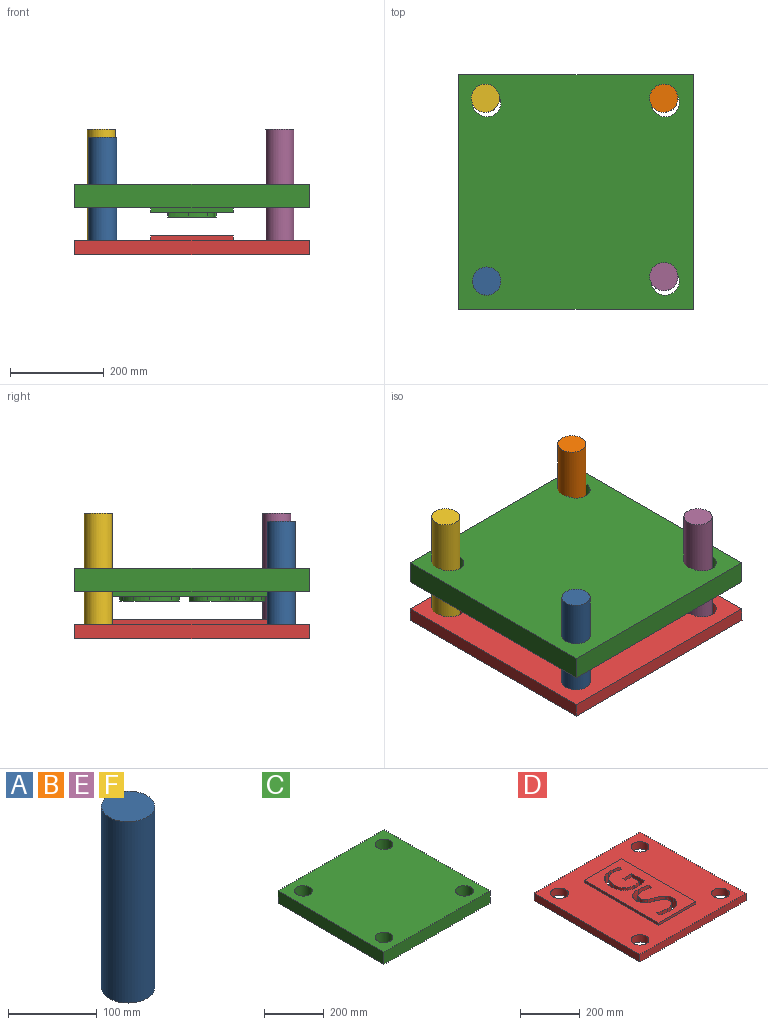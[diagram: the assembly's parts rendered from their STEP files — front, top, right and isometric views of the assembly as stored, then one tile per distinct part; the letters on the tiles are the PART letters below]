
ASSEMBLY  parts=6 mates=2
PART A: 3 faces, bbox 60x60x250 mm
  f0: cylinder r=30mm len=250mm, axis (0,0,-1), area 47123.9mm2, adj f1,f2
  f1: plane 60x60mm, normal (0,0,1), area 2827.4mm2, adj f0
  f2: plane 60x60mm, normal (0,0,-1), area 2827.4mm2, adj f0
PART B: same geometry as A
PART C: 62 faces, bbox 500x500x70 mm
  f0: plane 500x500mm, normal (0,0,-1), area 177440.3mm2, adj f1,f2,f3,f4,f5,f6,f7,f8
  f1: plane 500x50mm, normal (0,-1,0), area 25000mm2, adj f0,f2,f8,f9
  f2: plane 500x50mm, normal (1,0,0), area 25000mm2, adj f0,f1,f3,f9
  f3: plane 500x50mm, normal (0,1,0), area 25000mm2, adj f0,f2,f8,f9
  f4: cylinder r=30mm len=60mm, axis (0,0,1), area 9424.8mm2, adj f0,f9
  f5: cylinder r=30mm len=60mm, axis (0,0,1), area 9424.8mm2, adj f0,f9
  f6: cylinder r=30mm len=60mm, axis (0,0,1), area 9424.8mm2, adj f0,f9
  f7: cylinder r=30mm len=60mm, axis (0,0,1), area 9424.8mm2, adj f0,f9
  f8: plane 500x50mm, normal (-1,0,0), area 25000mm2, adj f0,f1,f3,f9
  f9: plane 500x500mm, normal (0,0,1), area 238690.3mm2, adj f1,f2,f3,f4,f5,f6,f7,f8
  f10: plane 175x10mm, normal (0,-1,0), area 1750mm2, adj f0,f11,f13,f14
  f11: plane 350x10mm, normal (1,0,0), area 3500mm2, adj f0,f10,f12,f14
  f12: plane 175x10mm, normal (0,1,0), area 1750mm2, adj f0,f11,f13,f14
  f13: plane 350x10mm, normal (-1,0,0), area 3500mm2, adj f0,f10,f12,f14
  f14: plane 350x175mm, normal (0,0,-1), area 50837.5mm2, adj f10,f11,f12,f13,f15,f16,f17,f18
  f15: plane 42.15x10mm, normal (0,1,0), area 421.5mm2, adj f14,f16,f26,f35
  f16: plane 12.89x10mm, normal (-1,0,0), area 128.9mm2, adj f14,f15,f27,f35
  f17: plane 12.73x10mm, normal (0.92,-0.4,0), area 139mm2, adj f14,f18,f34,f35
  f18: extruded ~36.99x10mm, area 379.6mm2, adj f14,f17,f19,f35
  f19: extruded ~34.15x10mm, area 353.5mm2, adj f14,f18,f20,f35
  f20: extruded ~22.35x22.21mm, area 320mm2, adj f14,f19,f21,f35
  f21: extruded ~33.9x10mm, area 351.3mm2, adj f14,f20,f22,f35
  f22: extruded ~46.94x15.69mm, area 507.1mm2, adj f14,f21,f23,f35
  f23: extruded ~43.83x16.76mm, area 483.3mm2, adj f14,f22,f24,f35
  f24: extruded ~23.58x10mm, area 236.6mm2, adj f14,f23,f25,f35
  f25: extruded ~20.03x10mm, area 206.1mm2, adj f14,f24,f26,f35
  f26: plane 60.3x10mm, normal (1,0,0), area 603mm2, adj f14,f15,f25,f35
  f27: plane 27.71x10mm, normal (0,-1,0), area 277.1mm2, adj f14,f16,f28,f35
  f28: plane 38.16x10mm, normal (-1,0,0), area 381.6mm2, adj f14,f27,f29,f35
  f29: extruded ~25.18x10mm, area 254.2mm2, adj f14,f28,f30,f35
  f30: extruded ~36x12.97mm, area 393.8mm2, adj f14,f29,f31,f35
  f31: extruded ~38.08x12.25mm, area 409.8mm2, adj f14,f30,f32,f35
  f32: extruded ~37.41x12.73mm, area 405.1mm2, adj f14,f31,f33,f35
  f33: extruded ~35.36x13.47mm, area 389.6mm2, adj f14,f32,f34,f35
  f34: extruded ~32.32x10mm, area 333.2mm2, adj f14,f17,f33,f35
  f35: plane 127.47x103.13mm, normal (0,0,-1), area 4654.5mm2, adj f15,f16,f17,f18,f19,f20,f21,f22
  f36: extruded ~32.48x15.1mm, area 372.1mm2, adj f14,f37,f48,f61
  f37: extruded ~26.31x10mm, area 285.9mm2, adj f14,f36,f38,f61
  f38: extruded ~34.14x18.99mm, area 394.1mm2, adj f14,f37,f49,f61
  f39: plane 15.95x10mm, normal (0.94,-0.34,0), area 169.5mm2, adj f14,f40,f54,f61
  f40: extruded ~43.25x10mm, area 444.3mm2, adj f14,f39,f41,f61
  f41: extruded ~36.26x10.79mm, area 385.6mm2, adj f14,f40,f42,f61
  f42: extruded ~29.01x13.69mm, area 333mm2, adj f14,f41,f43,f61
  f43: extruded ~28.15x10mm, area 303.7mm2, adj f14,f42,f44,f61
  f44: extruded ~31.43x18.66mm, area 369.3mm2, adj f14,f43,f55,f61
  f45: extruded ~21.16x10mm, area 221.6mm2, adj f14,f46,f60,f61
  f46: plane 17.67x10mm, normal (-1,0,0), area 176.7mm2, adj f14,f45,f47,f61
  f47: extruded ~43.15x10mm, area 441mm2, adj f14,f46,f48,f61
  f48: extruded ~40.99x11.67mm, area 434.1mm2, adj f14,f36,f47,f61
  f49: extruded ~21.96x10mm, area 240.2mm2, adj f14,f38,f50,f61
  f50: extruded ~10.2x10mm, area 141.6mm2, adj f14,f49,f51,f61
  f51: extruded ~13.43x10mm, area 139.2mm2, adj f14,f50,f52,f61
  f52: extruded ~17.36x10mm, area 199.6mm2, adj f14,f51,f53,f61
  f53: extruded ~22.77x10mm, area 240.3mm2, adj f14,f52,f54,f61
  f54: extruded ~37.97x10mm, area 391mm2, adj f14,f39,f53,f61
  f55: extruded ~23.46x10.03mm, area 255.4mm2, adj f14,f44,f56,f61
  f56: extruded ~11.01x10mm, area 147.9mm2, adj f14,f55,f57,f61
  f57: extruded ~13.41x10mm, area 139.9mm2, adj f14,f56,f58,f61
  f58: extruded ~19.38x10mm, area 223.6mm2, adj f14,f57,f59,f61
  f59: extruded ~27.62x10mm, area 289.6mm2, adj f14,f58,f60,f61
  f60: extruded ~22.65x10mm, area 228.1mm2, adj f14,f45,f59,f61
  f61: plane 162.14x99.25mm, normal (0,0,-1), area 5758mm2, adj f36,f37,f38,f39,f40,f41,f42,f43
PART D: 64 faces, bbox 500x500x40 mm
  f0: plane 500x30mm, normal (0,-1,0), area 15000mm2, adj f1,f7,f8,f9
  f1: plane 500x30mm, normal (1,0,0), area 15000mm2, adj f0,f2,f8,f9
  f2: plane 500x30mm, normal (0,1,0), area 15000mm2, adj f1,f7,f8,f9
  f3: cylinder r=30mm len=60mm, axis (0,0,-1), area 5654.9mm2, adj f8,f9
  f4: cylinder r=30mm len=60mm, axis (0,0,-1), area 5654.9mm2, adj f8,f9
  f5: cylinder r=30mm len=60mm, axis (0,0,-1), area 5654.9mm2, adj f8,f9
  f6: cylinder r=30mm len=60mm, axis (0,0,-1), area 5654.9mm2, adj f8,f9
  f7: plane 500x30mm, normal (-1,0,0), area 15000mm2, adj f0,f2,f8,f9
  f8: plane 500x500mm, normal (0,0,1), area 177440.3mm2, adj f0,f1,f2,f3,f4,f5,f6,f7
  f9: plane 500x500mm, normal (0,0,-1), area 228277.8mm2, adj f0,f1,f2,f3,f4,f5,f6,f7
  f10: plane 175x10mm, normal (0,-1,0), area 1750mm2, adj f8,f11,f62,f63
  f11: plane 350x10mm, normal (1,0,0), area 3500mm2, adj f8,f10,f12,f63
  f12: plane 175x10mm, normal (0,1,0), area 1750mm2, adj f8,f11,f62,f63
  f13: extruded ~40x20.65mm, area 916mm2, adj f9,f14,f60,f63
  f14: extruded ~40x20.34mm, area 820.3mm2, adj f9,f13,f15,f63
  f15: extruded ~40x26.83mm, area 1078.4mm2, adj f9,f14,f16,f63
  f16: extruded ~40x16.32mm, area 685.5mm2, adj f9,f15,f17,f63
  f17: plane 40x17.67mm, normal (1,0,0), area 707mm2, adj f9,f16,f18,f63
  f18: extruded ~40x21.16mm, area 886.3mm2, adj f9,f17,f19,f63
  f19: extruded ~40x22.65mm, area 912.4mm2, adj f9,f18,f20,f63
  f20: extruded ~40x27.62mm, area 1158.3mm2, adj f9,f19,f21,f63
  f21: extruded ~40x19.38mm, area 894.3mm2, adj f9,f20,f22,f63
  f22: extruded ~40x13.41mm, area 559.8mm2, adj f9,f21,f23,f63
  f23: extruded ~40x11.01mm, area 591.8mm2, adj f9,f22,f24,f63
  f24: extruded ~40x23.46mm, area 1021.6mm2, adj f9,f23,f25,f63
  f25: extruded ~40x31.43mm, area 1477mm2, adj f9,f24,f26,f63
  f26: extruded ~40x28.15mm, area 1214.7mm2, adj f9,f25,f27,f63
  f27: extruded ~40x29.01mm, area 1331.9mm2, adj f9,f26,f28,f63
  f28: extruded ~40x36.26mm, area 1542.4mm2, adj f9,f27,f29,f63
  f29: extruded ~43.25x40mm, area 1777mm2, adj f9,f28,f30,f63
  f30: plane 40x15.95mm, normal (-0.94,0.34,0), area 677.9mm2, adj f9,f29,f31,f63
  f31: extruded ~40x37.97mm, area 1564.1mm2, adj f9,f30,f32,f63
  f32: extruded ~40x22.77mm, area 961.2mm2, adj f9,f31,f33,f63
  f33: extruded ~40x17.36mm, area 798.3mm2, adj f9,f32,f34,f63
  f34: extruded ~40x13.43mm, area 556.8mm2, adj f9,f33,f35,f63
  f35: extruded ~40x10.2mm, area 566.5mm2, adj f9,f34,f36,f63
  f36: extruded ~40x21.96mm, area 960.7mm2, adj f9,f35,f37,f63
  f37: extruded ~40x34.14mm, area 1576.2mm2, adj f9,f36,f38,f63
  f38: extruded ~40x26.31mm, area 1143.6mm2, adj f9,f37,f60,f63
  f39: extruded ~40x12.11mm, area 485.5mm2, adj f9,f40,f61,f63
  f40: extruded ~40x24.88mm, area 1032.8mm2, adj f9,f39,f41,f63
  f41: plane 40x12.73mm, normal (-0.92,0.4,0), area 556.1mm2, adj f9,f40,f42,f63
  f42: extruded ~40x32.32mm, area 1332.7mm2, adj f9,f41,f43,f63
  f43: extruded ~40x35.36mm, area 1558.6mm2, adj f9,f42,f44,f63
  f44: extruded ~40x37.41mm, area 1620.3mm2, adj f9,f43,f45,f63
  f45: extruded ~40x38.08mm, area 1639.3mm2, adj f9,f44,f46,f63
  f46: extruded ~40x36mm, area 1575.3mm2, adj f9,f45,f47,f63
  f47: extruded ~40x25.18mm, area 1016.9mm2, adj f9,f46,f48,f63
  f48: plane 40x38.16mm, normal (1,0,0), area 1526.3mm2, adj f9,f47,f49,f63
  f49: plane 40x27.71mm, normal (0,1,0), area 1108.3mm2, adj f9,f48,f50,f63
  f50: plane 40x12.89mm, normal (1,0,0), area 515.6mm2, adj f9,f49,f51,f63
  f51: plane 42.15x40mm, normal (0,-1,0), area 1685.8mm2, adj f9,f50,f52,f63
  f52: plane 60.3x40mm, normal (-1,0,0), area 2412.1mm2, adj f9,f51,f53,f63
  f53: extruded ~40x20.03mm, area 824.3mm2, adj f9,f52,f54,f63
  f54: extruded ~40x23.58mm, area 946.5mm2, adj f9,f53,f55,f63
  f55: extruded ~43.83x40mm, area 1933.3mm2, adj f9,f54,f56,f63
  f56: extruded ~46.94x40mm, area 2028.4mm2, adj f9,f55,f57,f63
  f57: extruded ~40x33.9mm, area 1405.2mm2, adj f9,f56,f58,f63
  f58: extruded ~40x22.35mm, area 1280mm2, adj f9,f57,f59,f63
  f59: extruded ~40x22.74mm, area 956.3mm2, adj f9,f58,f61,f63
  f60: extruded ~40x32.48mm, area 1488.4mm2, adj f9,f13,f38,f63
  f61: extruded ~40x11.41mm, area 457.7mm2, adj f9,f39,f59,f63
  f62: plane 350x10mm, normal (-1,0,0), area 3500mm2, adj f8,f10,f12,f63
  f63: plane 350x175mm, normal (0,0,1), area 50837.5mm2, adj f10,f11,f12,f13,f14,f15,f16,f17
PART E: same geometry as A
PART F: same geometry as A
PLACE A rot(axis=(-0.52,0.24,0.82),0deg) t=(-284.29,-194.81,-70.57)mm
PLACE B t=(92.81,194.68,-53.8)mm
PLACE C rot(axis=(-0.52,0.24,0.82),0deg) t=(-94.29,-4.81,-45.57)mm
PLACE D rot(axis=(-0.52,0.24,0.82),0deg) t=(-94.29,-4.81,-195.57)mm
PLACE E t=(92.81,-185.32,-53.8)mm
PLACE F t=(-287.19,194.68,-53.8)mm
MATE fastened C.f6 <-> A.f0  axis (0,0,1) through (-284.29,-194.81,-70.57)mm
MATE fastened D.f4 <-> A.f0  axis (0,0,-1) through (-284.29,-194.81,-195.57)mm
